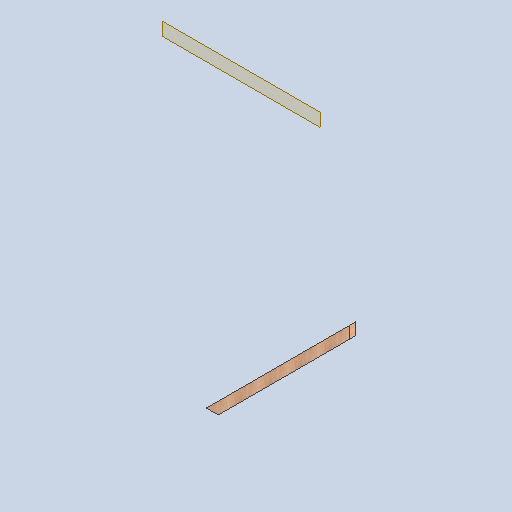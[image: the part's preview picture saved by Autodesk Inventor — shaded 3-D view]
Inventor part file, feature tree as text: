
AUTODESK INVENTOR PART (.ipt)
format: ipt  version: 2025 (Build 290162000, 162)  size: 86,016 bytes
history: native  units: in
note: dims shown in document units (in); Inventor stores cm internally (conversion verified against a paired STEP export)
features: other x3, sketch x1, plane x1
ambient origin geometry x8: Origin, YZ Plane, XZ Plane, XY Plane, X Axis, Y Axis, Z Axis, Center Point
bodies: Solid1 (feature_tree)
feature tree (5):
  other  "Leg slant.2.ipt"
  other  "Solid1::Leg slant.2.ipt"
  other  "TaggingFeature1"
  sketch  "Sketch1"  dims[d0=0.3937in]
  plane  "Work Plane1"
